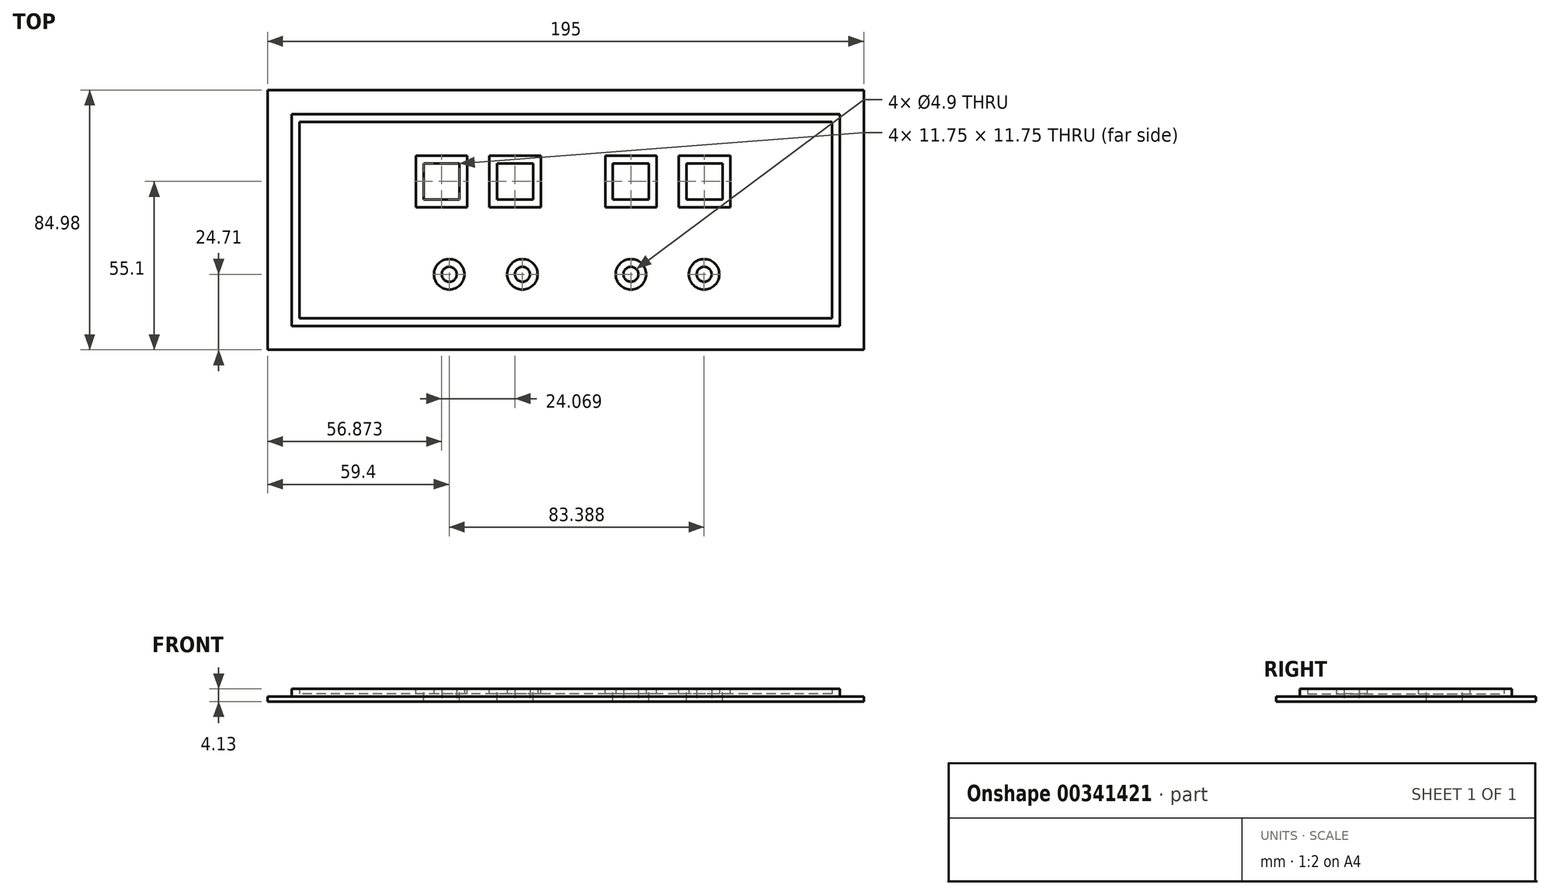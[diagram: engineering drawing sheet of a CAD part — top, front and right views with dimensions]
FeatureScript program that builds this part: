
annotation { "Feature Type Name" : "Feature", "Feature Type Description" : "" }
export const myFeature = defineFeature(function(context is Context, id is Id, definition is map)
    precondition{}
    {
        {
            var Q0;
            Q0=qCreatedBy(makeId("Top.planeOp"),FACE);
            var sketch = newSketch(context, id + "F0", { "sketchPlane" : qUnion([Q0])});
            skLineSegment(sketch, "E0.bottom", {"start": v(-97.5, 42.5) * mm, "end": v(97.5, 42.5) * mm});
            skLineSegment(sketch, "E0.top", {"start": v(-97.5, -42.5) * mm, "end": v(97.5, -42.5) * mm});
            skLineSegment(sketch, "E0.left", {"start": v(-97.5, 42.5) * mm, "end": v(-97.5, -42.5) * mm});
            skLineSegment(sketch, "E0.right", {"start": v(97.5, 42.5) * mm, "end": v(97.5, -42.5) * mm});
            skPoint(sketch, "E0.middle", {"position": v(0, 0) * mm});
            skSolve(sketch);
        }
        {
            var Q0;
            Q0 = qSketchRegion(id + "F0", true);
            extrude(context, id + "F1", {"entities" : qUnion([Q0]), "depth" : 1.59 * mm});
        }
        {
            var Q0;
            Q0=makeQuery(id+"F1.opExtrude","CAP_FACE",FACE,{"disambiguationData":[OSD([sQuery(id+"F0.wireOp",EDGE,"E0.bottom"),sQuery(id+"F0.wireOp",EDGE,"E0.top"),sQuery(id+"F0.wireOp",EDGE,"E0.left"),sQuery(id+"F0.wireOp",EDGE,"E0.right")])],"isStart":false});
            var sketch = newSketch(context, id + "F2", { "sketchPlane" : qUnion([Q0])});
            skLineSegment(sketch, "E1.bottom", {"start": v(-81.78, 25.9) * mm, "end": v(-17.33, 25.9) * mm});
            skLineSegment(sketch, "E1.top", {"start": v(-81.78, 14.29) * mm, "end": v(-17.33, 14.29) * mm});
            skLineSegment(sketch, "E1.left", {"start": v(-81.78, 25.9) * mm, "end": v(-81.78, 14.29) * mm});
            skLineSegment(sketch, "E1.right", {"start": v(-17.33, 25.9) * mm, "end": v(-17.33, 14.29) * mm});
            skPoint(sketch, "E1.middle", {"position": v(-49.55, 20.1) * mm});
            skLineSegment(sketch, "E2.bottom", {"start": v(-89.67, 34.67) * mm, "end": v(89.67, 34.67) * mm});
            skLineSegment(sketch, "E2.top", {"start": v(-89.67, -34.67) * mm, "end": v(89.67, -34.67) * mm});
            skLineSegment(sketch, "E2.left", {"start": v(-89.67, 34.67) * mm, "end": v(-89.67, -34.67) * mm});
            skLineSegment(sketch, "E2.right", {"start": v(89.67, 34.67) * mm, "end": v(89.67, -34.67) * mm});
            skSolve(sketch);
        }
        {
            var Q0;
            Q0 = qSketchRegion(id + "F2", true);
            var Q1;
            Q1=makeQuery(id+"F2.imprint","IMPRINT",FACE,{"disambiguationData":[TD([[makeQuery(id+"F2.imprint","IMPRINT",EDGE,{"derivedFrom":sQuery(id+"F2.wireOp",EDGE,"E1.bottom")}),1.0]])]});
            var Q2;
            Q2=makeQuery(id+"F2.imprint","IMPRINT",FACE,{"disambiguationData":[TD([[makeQuery(id+"F2.imprint","IMPRINT",EDGE,{"derivedFrom":sQuery(id+"F2.wireOp",EDGE,"E1.bottom")}),-1.0]])]});
            extrude(context, id + "F3", {"entities" : qUnion([Q0, Q1, Q2]), "operationType" : NewBodyOperationType.ADD, "depth" : 2.54 * mm});
        }
        {
            var Q0;
            Q0=makeQuery(id+"F1.opExtrude","CAP_FACE",FACE,{"disambiguationData":[OSD([sQuery(id+"F0.wireOp",EDGE,"E0.bottom"),sQuery(id+"F0.wireOp",EDGE,"E0.top"),sQuery(id+"F0.wireOp",EDGE,"E0.left"),sQuery(id+"F0.wireOp",EDGE,"E0.right")])],"isStart":true});
            var sketch = newSketch(context, id + "F4", { "sketchPlane" : qUnion([Q0])});
            skLineSegment(sketch, "E3", {"start": v(-76.55, 0) * mm, "end": v(75.91, 0) * mm});
            skLineSegment(sketch, "E4", {"start": v(-59.42, -42.5) * mm, "end": v(-59.42, -40.81) * mm});
            skCircle(sketch, "E5", {"center": v(-38.1, 17.78) * mm, "radius": 2.45 * mm});
            skCircle(sketch, "E6", {"center": v(45.29, 17.78) * mm, "radius": 2.45 * mm});
            skCircle(sketch, "E7", {"center": v(21.34, 17.78) * mm, "radius": 2.45 * mm});
            skCircle(sketch, "E8", {"center": v(-14.15, 17.78) * mm, "radius": 2.45 * mm});
            skSolve(sketch);
        }
        {
            var Q0;
            Q0 = qSketchRegion(id + "F4", true);
            extrude(context, id + "F5", {"entities" : qUnion([Q0]), "operationType" : NewBodyOperationType.REMOVE, "oppositeDirection" : true, "depth" : 22.86 * mm});
        }
        {
            var Q0;
            Q0=makeQuery(id+"F3.opExtrude","CAP_FACE",FACE,{"disambiguationData":[OSD([sQuery(id+"F2.wireOp",EDGE,"E2.bottom"),sQuery(id+"F2.wireOp",EDGE,"E2.top"),sQuery(id+"F2.wireOp",EDGE,"E2.left"),sQuery(id+"F2.wireOp",EDGE,"E2.right")])],"isStart":false});
            var sketch = newSketch(context, id + "F6", { "sketchPlane" : qUnion([Q0])});
            skLineSegment(sketch, "E9.bottom", {"start": v(51.28, 6.73) * mm, "end": v(39.53, 6.73) * mm});
            skLineSegment(sketch, "E9.top", {"start": v(51.28, 18.48) * mm, "end": v(39.53, 18.48) * mm});
            skLineSegment(sketch, "E9.left", {"start": v(51.28, 6.73) * mm, "end": v(51.28, 18.48) * mm});
            skLineSegment(sketch, "E9.right", {"start": v(39.53, 6.73) * mm, "end": v(39.53, 18.48) * mm});
            skPoint(sketch, "E9.middle", {"position": v(45.4, 12.6) * mm});
            skLineSegment(sketch, "E10.bottom", {"start": v(27.21, 6.74) * mm, "end": v(15.46, 6.74) * mm});
            skLineSegment(sketch, "E10.top", {"start": v(27.21, 18.49) * mm, "end": v(15.46, 18.49) * mm});
            skLineSegment(sketch, "E10.left", {"start": v(27.21, 6.74) * mm, "end": v(27.21, 18.49) * mm});
            skLineSegment(sketch, "E10.right", {"start": v(15.46, 6.74) * mm, "end": v(15.46, 18.49) * mm});
            skPoint(sketch, "E10.middle", {"position": v(21.34, 12.61) * mm});
            skPoint(sketch, "E11.middle", {"position": v(-16.45, 11) * mm});
            skPoint(sketch, "E12.middle", {"position": v(-40.4, 10.98) * mm});
            skLineSegment(sketch, "E13.bottom", {"start": v(-10.68, 6.74) * mm, "end": v(-22.43, 6.74) * mm});
            skLineSegment(sketch, "E13.top", {"start": v(-10.68, 18.49) * mm, "end": v(-22.43, 18.49) * mm});
            skLineSegment(sketch, "E13.left", {"start": v(-10.68, 6.74) * mm, "end": v(-10.68, 18.49) * mm});
            skLineSegment(sketch, "E13.right", {"start": v(-22.43, 6.74) * mm, "end": v(-22.43, 18.49) * mm});
            skPoint(sketch, "E13.middle", {"position": v(-16.56, 12.61) * mm});
            skLineSegment(sketch, "E14.bottom", {"start": v(-34.75, 6.74) * mm, "end": v(-46.5, 6.74) * mm});
            skLineSegment(sketch, "E14.top", {"start": v(-34.75, 18.49) * mm, "end": v(-46.5, 18.49) * mm});
            skLineSegment(sketch, "E14.left", {"start": v(-34.75, 6.74) * mm, "end": v(-34.75, 18.49) * mm});
            skLineSegment(sketch, "E14.right", {"start": v(-46.5, 6.74) * mm, "end": v(-46.5, 18.49) * mm});
            skPoint(sketch, "E14.middle", {"position": v(-40.63, 12.61) * mm});
            skSolve(sketch);
        }
        {
            var Q0;
            Q0 = qSketchRegion(id + "F6", true);
            extrude(context, id + "F7", {"entities" : qUnion([Q0]), "operationType" : NewBodyOperationType.REMOVE, "oppositeDirection" : true, "depth" : 25.4 * mm});
        }
        {
            var Q0;
            Q0=makeQuery(id+"F3.opExtrude","CAP_FACE",FACE,{"disambiguationData":[OSD([sQuery(id+"F2.wireOp",EDGE,"E2.bottom"),sQuery(id+"F2.wireOp",EDGE,"E2.top"),sQuery(id+"F2.wireOp",EDGE,"E2.left"),sQuery(id+"F2.wireOp",EDGE,"E2.right")])],"isStart":false});
            shell(context, id + "F8", {"entities" : qUnion([Q0]), "thickness" : 2.54 * mm});
        }
    });
